# Revit family: 3L-P-D
name_source: partatom
category: Lighting Fixtures
units: mm (PartAtom-declared; Revit-internal decimal feet)

## family parameters
Cut with Voids When Loaded = No
Host = Face
Light Source = Yes
OmniClass Number = 23.80.70.11.14.17
OmniClass Title = Direct/Indirect
Part Type = Normal
Room Calculation Point = No
Round Connector Dimension = Use Diameter
Shared = No

## types (5) — shared parameters
Color Filter = 16777215
Connector Description = Lighting Connector
Default Elevation = 48"
Description = MOD 3 LED Pendant Direct
Dimming Lamp Color Temperature Shift = <None>
Downlight diffuser = Soft Diffuse Lens
Emit Shape Visible in Rendering = No
Emit from Rectangle Length = 35"
Emit from Rectangle Width = 3"
Fixture distribution = Direct
Lamp = LED
Length = 36"
Load Classification = Lighting
Manufacturer = Litecontrol
Model = 3L-P-D
Pendent Height = 12"
Power Factor = 1
Reflector Finish = White Glass
Tilt Angle = -90.00°
URL = https://www.currentlighting.com
Voltage = 120 V
Wattage Comments = Variable Intensity technology provides specifiable lumen output/wattage

## per-type parameters (varying)
| type | Apparent Load | Finish Option | Photometric Web File | Product Material | Watts |
| 3L-P-D-4-SOF-X-CX-35K-D120 | 12 VA | 3L-P : Light Silver | 3L-P-D-4-SOF-X-CX-35K-D120.IES | Paint -Textured Camera Black | 12 W |
| 3L-P-D-4-SOF-X-CX-35K-D100 | 10 VA | 3L-P : Light Silver | 3L-P-D-4-SOF-X-CX-35K-D100.IES | Paint -Textured Camera Black | 10 W |
| 3L-P-D-4-SOF-X-CX-35K-D090 | 9 VA | 3L-P : Light Silver | 3L-P-D-4-SOF-X-CX-35K-D090.IES | Paint -Textured Camera Black | 9 W |
| 3L-P-D-4-SOF-X-CX-35K-D030 | 3 VA | 3L-P : Matte White | 3L-P-D-4-SOF-X-CX-35K-D030.IES | Textured Camera Black | 3 W |
| 3L-P-D-4-SOF-X-CX-35K-D060 | 6 VA | 3L-P : Light Silver | 3L-P-D-4-SOF-X-CX-35K-D060.IES | Paint -Textured Camera Black | 6 W |

## geometry (parser evidence)
native form markers: Blend x11, Sweep x5
no freeform markers — native parametric forms only
